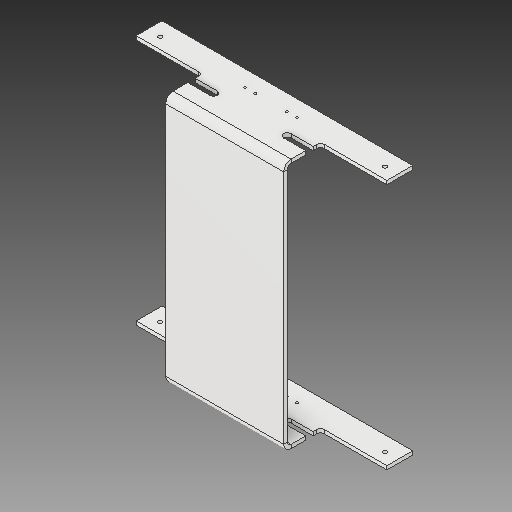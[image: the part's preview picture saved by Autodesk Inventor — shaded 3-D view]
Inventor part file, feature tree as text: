
AUTODESK INVENTOR PART (.ipt)
format: ipt  version: 2018 (Build 220112000, 112)  size: 134,144 bytes
history: native  units: in
note: dims shown in document units (in); Inventor stores cm internally (conversion verified against a paired STEP export)
features: fillet x1
ambient origin geometry x8: Origin, YZ Plane, XZ Plane, XY Plane, X Axis, Y Axis, Z Axis, Center Point
bodies: Solid1 (feature_tree)
feature tree (1):
  fillet  "Fillet2"  [1 undecoded]
note: 1 required parameter value undecoded (feature->parameter linkage not recoverable at this tier; creation-order binding heuristic only, values carry confidence <= 0.55)
